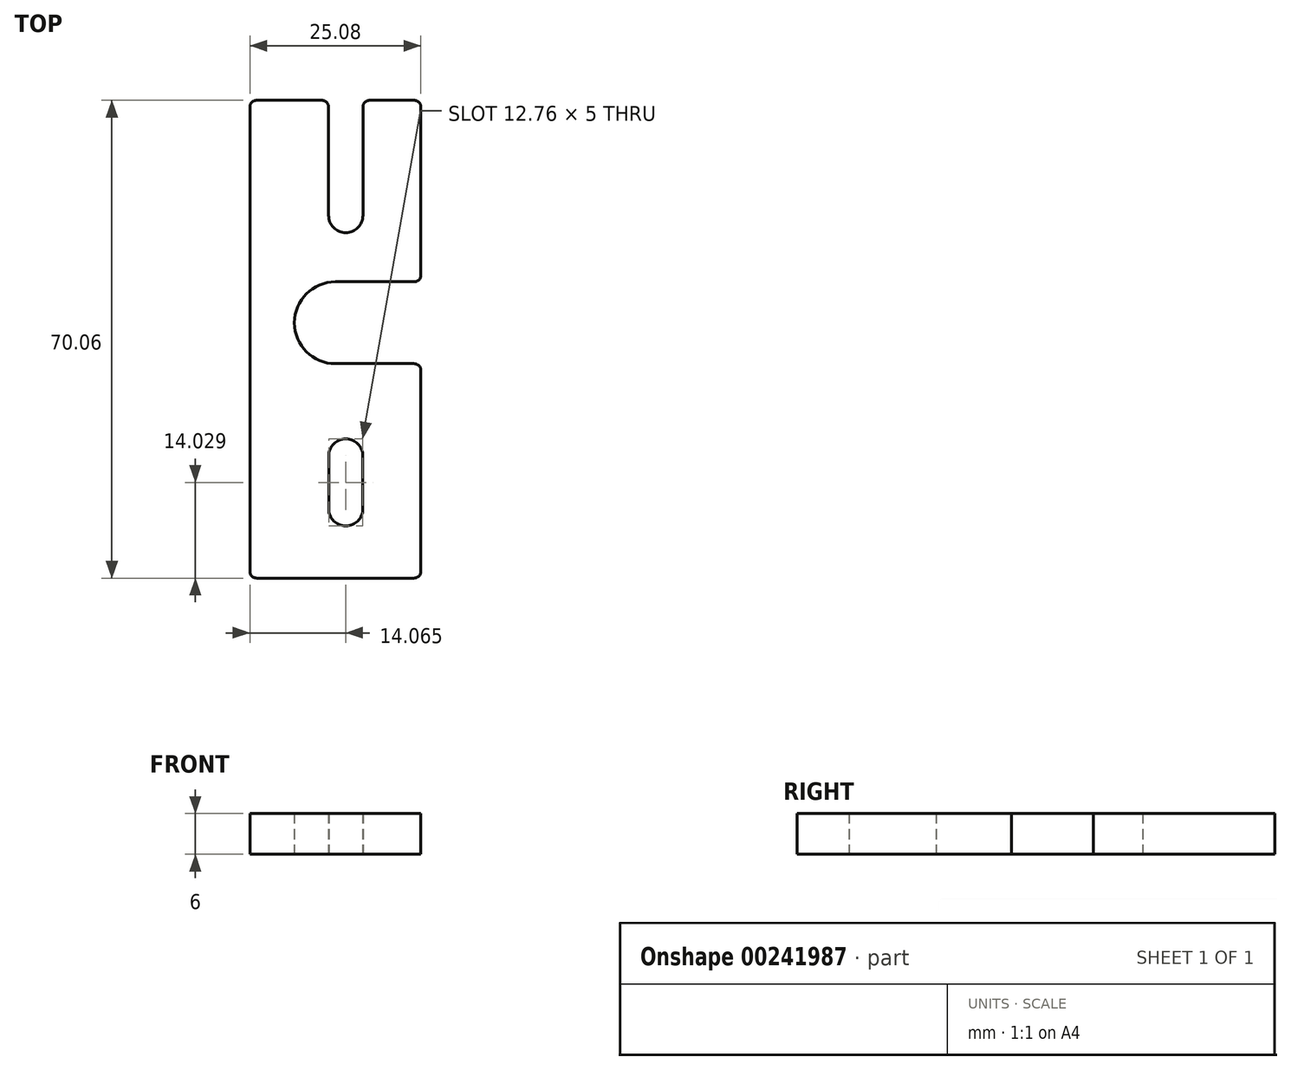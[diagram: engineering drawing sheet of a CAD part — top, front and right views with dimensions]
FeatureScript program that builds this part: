
annotation { "Feature Type Name" : "Feature", "Feature Type Description" : "" }
export const myFeature = defineFeature(function(context is Context, id is Id, definition is map)
    precondition{}
    {
        {
            var Q0;
            Q0=qCreatedBy(makeId("Top.planeOp"),FACE);
            var sketch = newSketch(context, id + "F0", { "sketchPlane" : qUnion([Q0])});
            skLineSegment(sketch, "E0.bottom", {"start": v(-12.54, 35.03) * mm, "end": v(12.54, 35.03) * mm});
            skLineSegment(sketch, "E0.top", {"start": v(-12.54, -35.03) * mm, "end": v(12.54, -35.03) * mm});
            skLineSegment(sketch, "E0.left", {"start": v(-12.54, 35.03) * mm, "end": v(-12.54, -35.03) * mm});
            skLineSegment(sketch, "E0.right", {"start": v(12.54, 35.03) * mm, "end": v(12.54, -35.03) * mm});
            skPoint(sketch, "E0.middle", {"position": v(0, 0) * mm});
            skLineSegment(sketch, "E1", {"start": v(4.04, 35.03) * mm, "end": v(4.04, 18.14) * mm});
            skLineSegment(sketch, "E2", {"start": v(-1, 35.03) * mm, "end": v(-1, 18.14) * mm});
            skLineSegment(sketch, "E3", {"start": v(4.04, 18.14) * mm, "end": v(-1, 18.14) * mm});
            skCircle(sketch, "E4", {"center": v(1.52, 18.14) * mm, "radius": 2.51 * mm});
            skLineSegment(sketch, "E5", {"start": v(12.54, 8.41) * mm, "end": v(0, 8.41) * mm});
            skLineSegment(sketch, "E6", {"start": v(12.54, -3.59) * mm, "end": v(0, -3.59) * mm});
            skLineSegment(sketch, "E7", {"start": v(0, -3.59) * mm, "end": v(0, 8.41) * mm});
            skCircle(sketch, "E8", {"center": v(0, 2.41) * mm, "radius": 6 * mm});
            skLineSegment(sketch, "E9", {"start": v(1.52, -24.88) * mm, "end": v(1.52, -17.12) * mm});
            skArc(sketch, "E10.0.startCap", {"start": v(4.03, -24.88) * mm, "mid": v(1.53, -27.38) * mm, "end": v(-0.97, -24.88) * mm});
            skArc(sketch, "E10.0.endCap", {"start": v(-0.98, -17.12) * mm, "mid": v(1.52, -14.62) * mm, "end": v(4.02, -17.12) * mm});
            skLineSegment(sketch, "E10.0.left", {"start": v(-0.97, -24.88) * mm, "end": v(-0.97, -17.12) * mm});
            skLineSegment(sketch, "E10.0.right", {"start": v(4.03, -24.88) * mm, "end": v(4.03, -17.12) * mm});
            skSolve(sketch);
        }
        {
            var Q0;
            {var subQ3=sQuery(id+"F0.wireOp",EDGE,"E0.top");Q0=makeQuery(id+"F0.imprint","IMPRINT",FACE,{"disambiguationData":[TD([[makeQuery(id+"F0.imprint","IMPRINT",EDGE,{"derivedFrom":subQ3}),1.0]])]});}
            extrude(context, id + "F1", {"entities" : qUnion([Q0]), "depth" : 6 * mm});
        }
        {
            var Q0;
            Q0=makeQuery(id+"F1.opExtrude","SWEPT_EDGE",EDGE,{"disambiguationData":[OSD([sQuery(id+"F0.wireOp",EDGE,"E0.top"),sQuery(id+"F0.wireOp",EDGE,"E0.left")])]});
            var Q1;
            Q1=makeQuery(id+"F1.opExtrude","SWEPT_EDGE",EDGE,{"disambiguationData":[OSD([sQuery(id+"F0.wireOp",EDGE,"E0.bottom"),sQuery(id+"F0.wireOp",EDGE,"E0.left")])]});
            var Q2;
            Q2=makeQuery(id+"F1.opExtrude","SWEPT_EDGE",EDGE,{"disambiguationData":[OSD([sQuery(id+"F0.wireOp",EDGE,"E0.top"),sQuery(id+"F0.wireOp",EDGE,"E0.right")])]});
            var Q3;
            Q3=makeQuery(id+"F1.opExtrude","SWEPT_EDGE",EDGE,{"disambiguationData":[OSD([sQuery(id+"F0.wireOp",EDGE,"E0.bottom"),sQuery(id+"F0.wireOp",EDGE,"E0.right")])]});
            var Q4;
            Q4=makeQuery(id+"F1.opExtrude","SWEPT_EDGE",EDGE,{"disambiguationData":[OSD([sQuery(id+"F0.wireOp",EDGE,"E0.right"),sQuery(id+"F0.wireOp",EDGE,"E6")])]});
            var Q5;
            Q5=makeQuery(id+"F1.opExtrude","SWEPT_EDGE",EDGE,{"disambiguationData":[OSD([sQuery(id+"F0.wireOp",EDGE,"E0.right"),sQuery(id+"F0.wireOp",EDGE,"E5")])]});
            var Q6;
            Q6=makeQuery(id+"F1.opExtrude","SWEPT_EDGE",EDGE,{"disambiguationData":[OSD([sQuery(id+"F0.wireOp",EDGE,"E0.bottom"),sQuery(id+"F0.wireOp",EDGE,"E2")])]});
            var Q7;
            Q7=makeQuery(id+"F1.opExtrude","SWEPT_EDGE",EDGE,{"disambiguationData":[OSD([sQuery(id+"F0.wireOp",EDGE,"E0.bottom"),sQuery(id+"F0.wireOp",EDGE,"E1")])]});
            fillet(context, id + "F2", {"entities" : qUnion([Q0, Q1, Q2, Q3, Q4, Q5, Q6, Q7]), "radius" : 1 * mm, "tangentPropagation" : true, "allowEdgeOverflow" : false});
        }
    });
